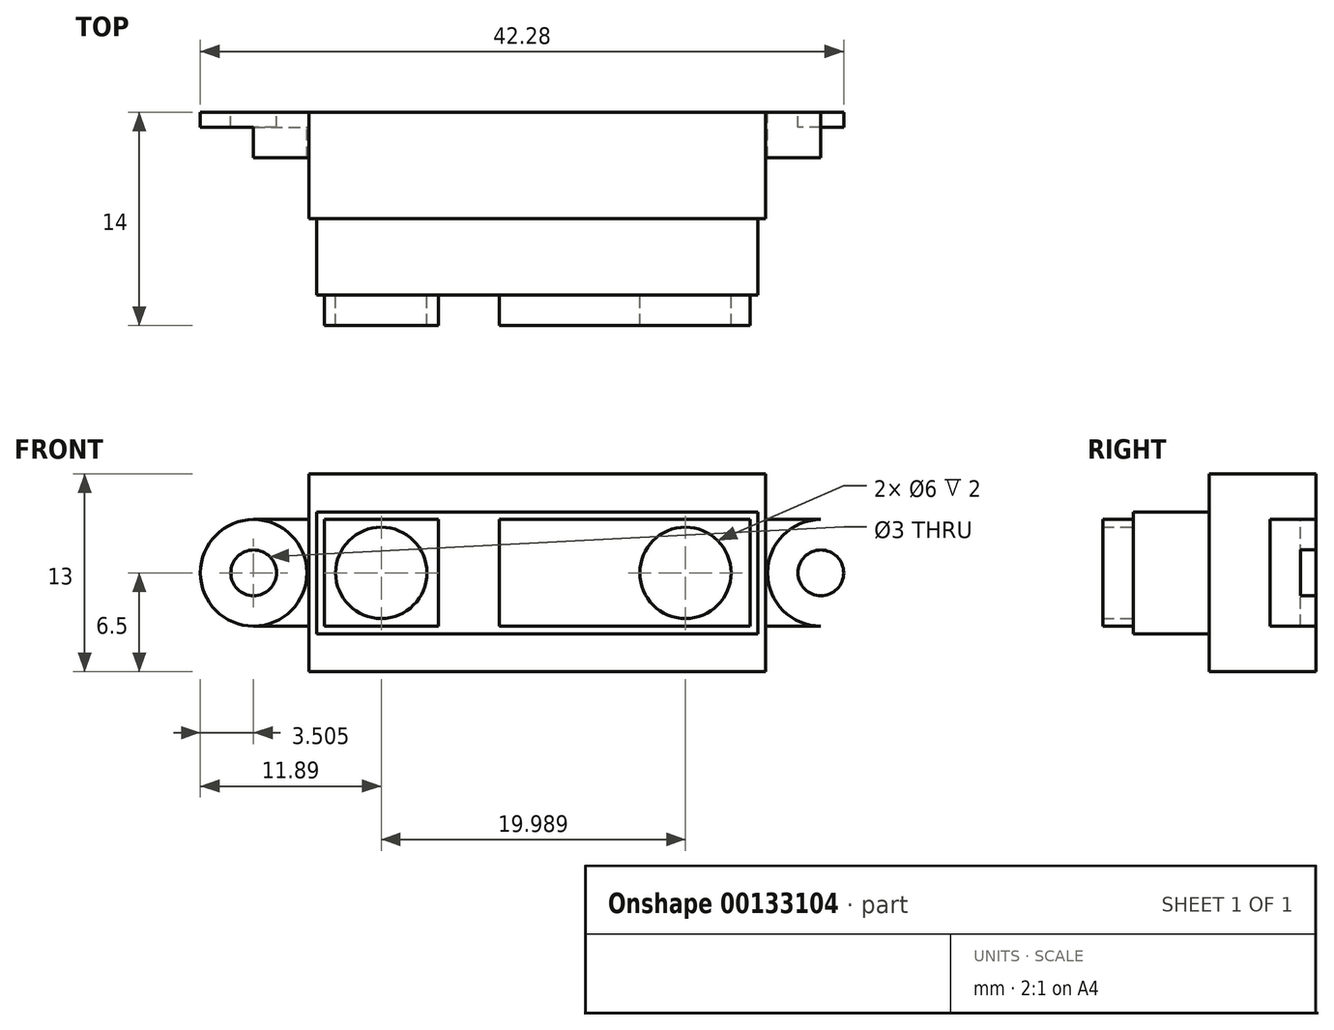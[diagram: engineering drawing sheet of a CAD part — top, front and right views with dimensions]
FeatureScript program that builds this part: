
annotation { "Feature Type Name" : "Feature", "Feature Type Description" : "" }
export const myFeature = defineFeature(function(context is Context, id is Id, definition is map)
    precondition{}
    {
        {
            var Q0;
            Q0=qCreatedBy(makeId("Front.planeOp"),FACE);
            var sketch = newSketch(context, id + "F0", { "sketchPlane" : qUnion([Q0])});
            skLineSegment(sketch, "E0.bottom", {"start": v(15, 6.5) * mm, "end": v(-15, 6.5) * mm});
            skLineSegment(sketch, "E0.top", {"start": v(15, -6.5) * mm, "end": v(-15, -6.5) * mm});
            skLineSegment(sketch, "E0.left", {"start": v(15, 6.5) * mm, "end": v(15, -6.5) * mm});
            skLineSegment(sketch, "E0.right", {"start": v(-15, 6.5) * mm, "end": v(-15, -6.5) * mm});
            skPoint(sketch, "E0.middle", {"position": v(0, 0) * mm});
            skLineSegment(sketch, "E1.bottom", {"start": v(-15, -3.5) * mm, "end": v(-18.64, -3.5) * mm});
            skLineSegment(sketch, "E1.top", {"start": v(-15, 3.5) * mm, "end": v(-18.64, 3.5) * mm});
            skLineSegment(sketch, "E1.left", {"start": v(-15, -3.5) * mm, "end": v(-15, 3.5) * mm});
            skArc(sketch, "E2", {"start": v(-18.64, 3.5) * mm, "mid": v(-22.14, 0) * mm, "end": v(-18.64, -3.5) * mm});
            skCircle(sketch, "E3", {"center": v(-18.64, 0) * mm, "radius": 1.5 * mm});
            skLineSegment(sketch, "E4.MirrorCS", {"start": v(15, 3.5) * mm, "end": v(18.64, 3.5) * mm});
            skCircle(sketch, "E5.MirrorC", {"center": v(18.64, 0) * mm, "radius": 1.5 * mm});
            skArc(sketch, "E6.MirrorCS", {"start": v(18.64, 3.5) * mm, "mid": v(22.14, 0) * mm, "end": v(18.64, -3.5) * mm});
            skLineSegment(sketch, "E7.MirrorCS", {"start": v(15, -3.5) * mm, "end": v(18.64, -3.5) * mm});
            skCircle(sketch, "E8", {"center": v(18.64, 0) * mm, "radius": 3.5 * mm});
            skCircle(sketch, "E9", {"center": v(-18.64, 0) * mm, "radius": 3.5 * mm});
            skSolve(sketch);
        }
        {
            var Q0;
            {var subQ3=sQuery(id+"F0.wireOp",EDGE,"E0.bottom");Q0=makeQuery(id+"F0.imprint","IMPRINT",FACE,{"disambiguationData":[TD([[makeQuery(id+"F0.imprint","IMPRINT",EDGE,{"derivedFrom":subQ3}),1.0]])]});}
            extrude(context, id + "F1", {"entities" : qUnion([Q0]), "depth" : 7 * mm});
        }
        {
            var Q0;
            Q0=makeQuery(id+"F1.opExtrude","CAP_FACE",FACE,{"disambiguationData":[OSD([sQuery(id+"F0.wireOp",EDGE,"E0.bottom"),sQuery(id+"F0.wireOp",EDGE,"E0.top"),sQuery(id+"F0.wireOp",EDGE,"E0.left"),sQuery(id+"F0.wireOp",EDGE,"E0.right")])],"isStart":false});
            var sketch = newSketch(context, id + "F2", { "sketchPlane" : qUnion([Q0])});
            skLineSegment(sketch, "E10.bottom", {"start": v(14.5, 4) * mm, "end": v(-14.5, 4) * mm});
            skLineSegment(sketch, "E10.top", {"start": v(14.5, -4) * mm, "end": v(-14.5, -4) * mm});
            skLineSegment(sketch, "E10.left", {"start": v(14.5, 4) * mm, "end": v(14.5, -4) * mm});
            skLineSegment(sketch, "E10.right", {"start": v(-14.5, 4) * mm, "end": v(-14.5, -4) * mm});
            skPoint(sketch, "E10.middle", {"position": v(0, 0) * mm});
            skSolve(sketch);
        }
        {
            var Q0;
            Q0 = qSketchRegion(id + "F2", true);
            extrude(context, id + "F3", {"entities" : qUnion([Q0]), "operationType" : NewBodyOperationType.ADD, "depth" : 5 * mm});
        }
        {
            var Q0;
            Q0=makeQuery(id+"F3.opExtrude","CAP_FACE",FACE,{"disambiguationData":[OSD([sQuery(id+"F2.wireOp",EDGE,"E10.bottom"),sQuery(id+"F2.wireOp",EDGE,"E10.top"),sQuery(id+"F2.wireOp",EDGE,"E10.left"),sQuery(id+"F2.wireOp",EDGE,"E10.right")])],"isStart":false});
            var sketch = newSketch(context, id + "F4", { "sketchPlane" : qUnion([Q0])});
            skLineSegment(sketch, "E11.bottom", {"start": v(-14, 3.5) * mm, "end": v(-6.5, 3.5) * mm});
            skLineSegment(sketch, "E11.top", {"start": v(-14, -3.5) * mm, "end": v(-6.5, -3.5) * mm});
            skLineSegment(sketch, "E11.left", {"start": v(-14, 3.5) * mm, "end": v(-14, -3.5) * mm});
            skLineSegment(sketch, "E11.right", {"start": v(-6.5, 3.5) * mm, "end": v(-6.5, -3.5) * mm});
            skLineSegment(sketch, "E12", {"start": v(-14, 0) * mm, "end": v(-6.5, 0) * mm});
            skCircle(sketch, "E13", {"center": v(-10.25, 0) * mm, "radius": 3 * mm});
            skLineSegment(sketch, "E14.bottom", {"start": v(-2.5, 3.5) * mm, "end": v(14, 3.5) * mm});
            skLineSegment(sketch, "E14.top", {"start": v(-2.5, -3.5) * mm, "end": v(14, -3.5) * mm});
            skLineSegment(sketch, "E14.left", {"start": v(-2.5, 3.5) * mm, "end": v(-2.5, -3.5) * mm});
            skLineSegment(sketch, "E14.right", {"start": v(14, 3.5) * mm, "end": v(14, -3.5) * mm});
            skCircle(sketch, "E15", {"center": v(9.74, 0) * mm, "radius": 3 * mm});
            skSolve(sketch);
        }
        {
            var Q0;
            {var subQ6=sQuery(id+"F4.wireOp",EDGE,"E11.bottom");Q0=makeQuery(id+"F4.imprint","IMPRINT",FACE,{"disambiguationData":[TD([[makeQuery(id+"F4.imprint","IMPRINT",EDGE,{"derivedFrom":subQ6}),-1.0]])]});}
            var Q1;
            {var subQ5=sQuery(id+"F4.wireOp",EDGE,"E11.top");Q1=makeQuery(id+"F4.imprint","IMPRINT",FACE,{"disambiguationData":[TD([[makeQuery(id+"F4.imprint","IMPRINT",EDGE,{"derivedFrom":subQ5}),1.0]])]});}
            var Q2;
            Q2=makeQuery(id+"F4.imprint","IMPRINT",FACE,{"disambiguationData":[TD([[makeQuery(id+"F4.imprint","IMPRINT",EDGE,{"derivedFrom":sQuery(id+"F4.wireOp",EDGE,"E14.bottom")}),-1.0]])]});
            extrude(context, id + "F5", {"entities" : qUnion([Q0, Q1, Q2]), "operationType" : NewBodyOperationType.ADD, "depth" : 2 * mm});
        }
        {
            var Q0;
            Q0=makeQuery(id+"F0.imprint","IMPRINT",FACE,{"disambiguationData":[TD([[makeQuery(id+"F0.imprint","IMPRINT",EDGE,{"derivedFrom":sQuery(id+"F0.wireOp",EDGE,"E1.bottom")}),-1.0]])]});
            var Q1;
            {var subQ0=sQuery(id+"F0.wireOp",EDGE,"E4.MirrorCS");Q1=makeQuery(id+"F0.imprint","IMPRINT",FACE,{"disambiguationData":[TD([[makeQuery(id+"F0.imprint","IMPRINT",EDGE,{"derivedFrom":subQ0}),-1.0]])]});}
            var Q2;
            Q2=makeQuery(id+"F0.imprint","IMPRINT",FACE,{"disambiguationData":[TD([[makeQuery(id+"F0.imprint","IMPRINT",EDGE,{"derivedFrom":sQuery(id+"F0.wireOp",EDGE,"E3")}),-1.0]])]});
            var Q3;
            Q3=makeQuery(id+"F0.imprint","IMPRINT",FACE,{"disambiguationData":[TD([[makeQuery(id+"F0.imprint","IMPRINT",EDGE,{"derivedFrom":sQuery(id+"F0.wireOp",EDGE,"E5.MirrorC")}),1.0]])]});
            extrude(context, id + "F6", {"entities" : qUnion([Q0, Q1, Q2, Q3]), "operationType" : NewBodyOperationType.ADD, "depth" : 1 * mm});
        }
        {
            var Q0;
            {var subQ0=sQuery(id+"F0.wireOp",EDGE,"E1.bottom");Q0=makeQuery(id+"F0.imprint","IMPRINT",FACE,{"disambiguationData":[TD([[makeQuery(id+"F0.imprint","IMPRINT",EDGE,{"derivedFrom":subQ0}),-1.0]])]});}
            var Q1;
            {var subQ0=sQuery(id+"F0.wireOp",EDGE,"E4.MirrorCS");Q1=makeQuery(id+"F0.imprint","IMPRINT",FACE,{"disambiguationData":[TD([[makeQuery(id+"F0.imprint","IMPRINT",EDGE,{"derivedFrom":subQ0}),-1.0]])]});}
            extrude(context, id + "F7", {"entities" : qUnion([Q0, Q1]), "operationType" : NewBodyOperationType.ADD, "depth" : 3 * mm});
        }
    });
